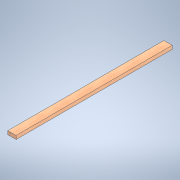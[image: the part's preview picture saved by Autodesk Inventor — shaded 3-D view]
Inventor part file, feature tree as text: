
AUTODESK INVENTOR PART (.ipt)
format: ipt  version: 2020.2 (Build 242310000, 310)  size: 101,888 bytes
history: native  units: in
note: dims shown in document units (in); Inventor stores cm internally (conversion verified against a paired STEP export)
features: extrude x1, sketch x1
ambient origin geometry x8: Origin, YZ Plane, XZ Plane, XY Plane, X Axis, Y Axis, Z Axis, Center Point
bodies: Solid1 (feature_tree)
feature tree (2):
  extrude  "Extrusion1"  [1 undecoded]
  sketch  "Sketch1"  dims[d3=0.0in]
note: 1 required parameter value undecoded (feature->parameter linkage not recoverable at this tier; creation-order binding heuristic only, values carry confidence <= 0.55)
